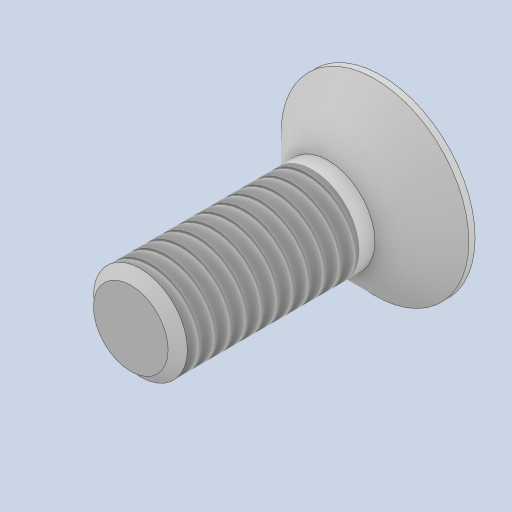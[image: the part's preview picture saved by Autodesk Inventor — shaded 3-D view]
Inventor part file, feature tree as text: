
AUTODESK INVENTOR PART (.ipt)
format: ipt  version: 2023 (Build 270158000, 158)  size: 199,680 bytes
history: native  units: mm
features: other x14, sketch x3, revolve x1, thread x1, hole x1, extrude x1
ambient origin geometry x8: Origin, YZ Plane, XZ Plane, XY Plane, X Axis, Y Axis, Z Axis, Center Point
bodies: Solid1 (feature_tree)
feature tree (21):
  revolve  "Revolution1"  [1 undecoded]
  thread  "Thread1"  [1 undecoded]
  hole  "Hole1"  [1 undecoded]
  extrude  "Extrusion1"  [1 undecoded]
  other  "bolt_to_nut_XY"
  other  "bolt_to_nut_YZ"
  other  "bolt_to_nut_ZX"
  other  "bolt_to_nut_X"
  other  "bolt_to_nut_Y"
  other  "bolt_to_nut_Z"
  other  "bolt_to_nut_Center"
  other  "dummy_to_bolt_XY"
  other  "dummy_to_bolt_YZ"
  other  "dummy_to_bolt_ZX"
  other  "dummy_to_bolt_X"
  other  "dummy_to_bolt_Y"
  other  "dummy_to_bolt_Z"
  other  "dummy_to_bolt_Center"
  sketch  "Sketch_1"  dims[d0=360.0deg d1=5.4935mm d2=0.0mm]
  sketch  "Sketch2"  dims[d3=2.0mm d4=6.0mm d5=4.0mm d6=2.0mm d7=90.0deg d8=0.85mm d9=150.0deg d10=0.85mm d11=0.0mm]
  sketch  "Sketch_3"  dims[d12=0.0mm]
note: 4 required parameter values undecoded (feature->parameter linkage not recoverable at this tier; creation-order binding heuristic only, values carry confidence <= 0.55)